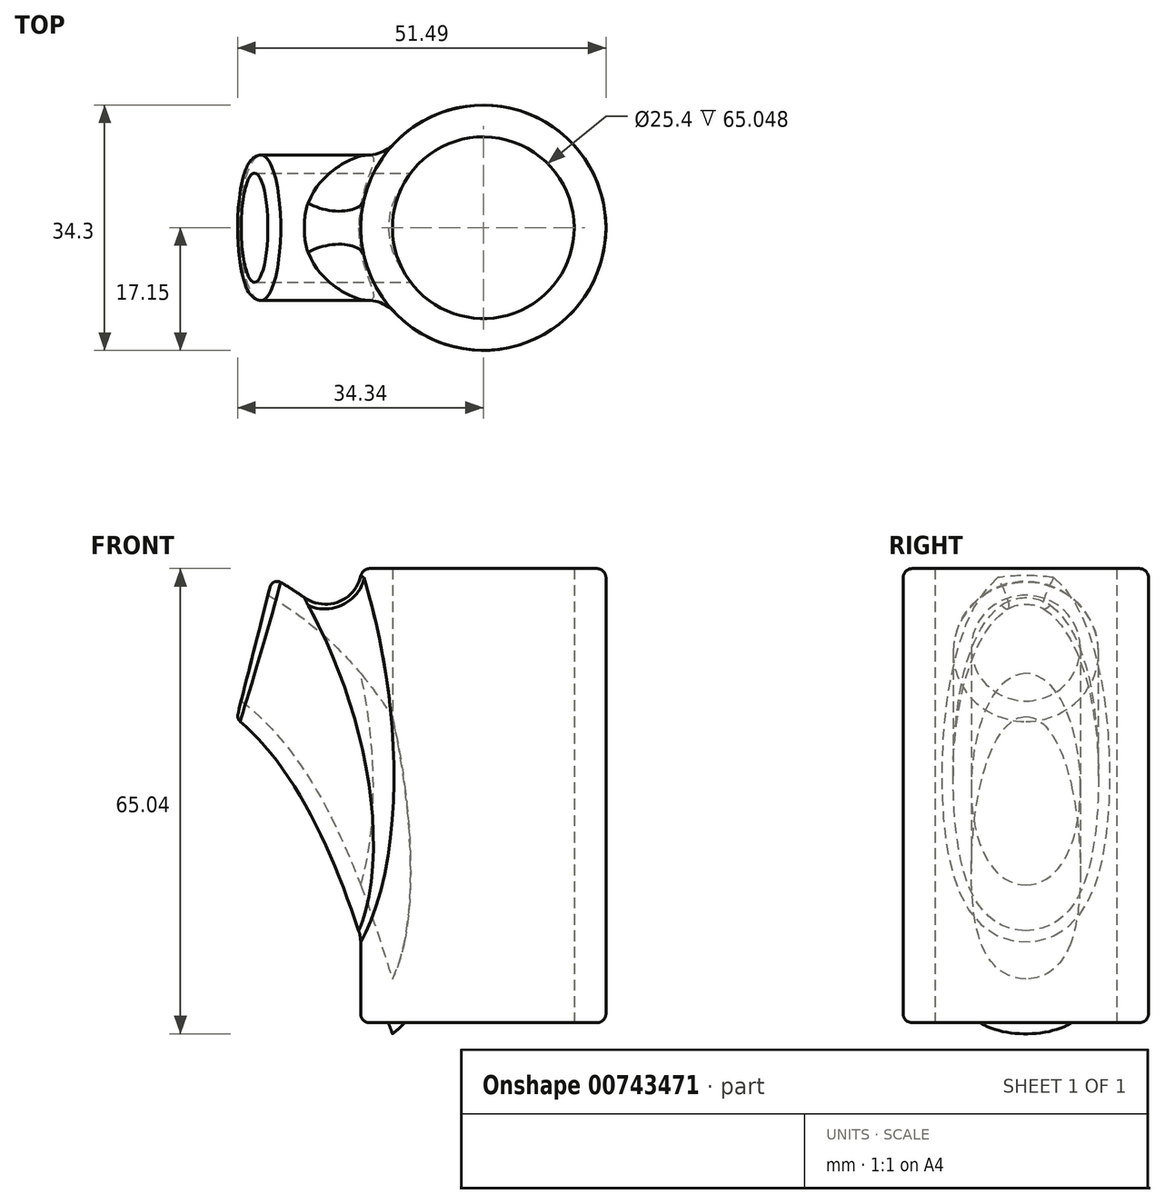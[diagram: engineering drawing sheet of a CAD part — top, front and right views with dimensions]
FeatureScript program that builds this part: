
annotation { "Feature Type Name" : "Feature", "Feature Type Description" : "" }
export const myFeature = defineFeature(function(context is Context, id is Id, definition is map)
    precondition{}
    {
        {
            var Q0;
            Q0=qCreatedBy(makeId("Top.planeOp"),FACE);
            var sketch = newSketch(context, id + "F0", { "sketchPlane" : qUnion([Q0])});
            skCircle(sketch, "E0", {"center": v(0, 0) * mm, "radius": 12.7 * mm});
            skCircle(sketch, "E1", {"center": v(0, 0) * mm, "radius": 17.15 * mm});
            skSolve(sketch);
        }
        {
            var Q0;
            Q0=makeQuery(id+"F0.imprint","IMPRINT",FACE,{"disambiguationData":[TD([[makeQuery(id+"F0.imprint","IMPRINT",EDGE,{"derivedFrom":sQuery(id+"F0.wireOp",EDGE,"E0")}),-1.0]])]});
            extrude(context, id + "F1", {"entities" : qUnion([Q0]), "depth" : 63.5 * mm, "offsetDistance" : 25.4 * mm});
        }
        {
            var Q0;
            Q0=qCreatedBy(makeId("Right.planeOp"),FACE);
            cPlane(context, id + "F2", {"entities" : qUnion([Q0]), "cplaneType" : CPlaneType.OFFSET, "offset" : 16.76 * mm, "oppositeDirection" : true, "width" : 152.4 * mm, "height" : 152.4 * mm});
        }
        {
            var Q0;
            Q0=qCreatedBy(id+"F2.planeOp",FACE);
            var sketch = newSketch(context, id + "F3", { "sketchPlane" : qUnion([Q0])});
            skLineSegment(sketch, "E2", {"start": v(45.22, 63.3) * mm, "end": v(-44.35, 63.3) * mm});
            skSolve(sketch);
        }
        {
            var Q0;
            Q0=sQuery(id+"F3.wireOp",EDGE,"E2");
            cPlane(context, id + "F4", {"entities" : qUnion([Q0]), "cplaneType" : CPlaneType.LINE_ANGLE, "offset" : 25.4 * mm, "angle" : 62.98 * degree, "width" : 152.4 * mm, "height" : 152.4 * mm});
        }
        {
            var Q0;
            Q0=qCreatedBy(id+"F4.planeOp",FACE);
            var sketch = newSketch(context, id + "F5", { "sketchPlane" : qUnion([Q0])});
            skCircle(sketch, "E3", {"center": v(0, 30.29) * mm, "radius": 7.62 * mm});
            skCircle(sketch, "E4", {"center": v(0, 30.29) * mm, "radius": 10.16 * mm});
            skSolve(sketch);
        }
        {
            var Q0;
            {var subQ0=sQuery(id+"F5.wireOp",EDGE,"E4");Q0=makeQuery(id+"FPSWW7IS3d8COEw_1.boolean.opBoolean","SPLIT",FACE,{"disambiguationData":[TD([makeQuery(id+"F1.opExtrude","SWEPT_FACE",FACE,{"disambiguationData":[OSD([sQuery(id+"F0.wireOp",EDGE,"E1")])]})])],"derivedFrom":makeQuery(id+"FPSWW7IS3d8COEw_1.opExtrude","SWEPT_FACE",FACE,{"disambiguationData":[OSD([subQ0])]})});}
            var Q1;
            Q1=makeQuery(id+"F1.opExtrude","CAP_EDGE",EDGE,{"disambiguationData":[OSD([sQuery(id+"F0.wireOp",EDGE,"E1")])],"isStart":false});
            var Q2;
            Q2=makeQuery(id+"F1.opExtrude","CAP_EDGE",EDGE,{"disambiguationData":[OSD([sQuery(id+"F0.wireOp",EDGE,"E1")])],"isStart":true});
            fillet(context, id + "F6", {"entities" : qUnion([Q0, Q1, Q2]), "radius" : 1.27 * mm, "tangentPropagation" : true, "allowEdgeOverflow" : false});
        }
        {
            var Q0;
            Q0=makeQuery(id+"F1.opExtrude","CAP_FACE",FACE,{"disambiguationData":[OSD([sQuery(id+"F0.wireOp",EDGE,"E0"),sQuery(id+"F0.wireOp",EDGE,"E1")])],"isStart":true});
            var sketch = newSketch(context, id + "F7", { "sketchPlane" : qUnion([Q0])});
            skCircle(sketch, "E5", {"center": v(0, 0) * mm, "radius": 12.7 * mm});
            skSolve(sketch);
        }
        {
            var Q0;
            Q0=qSketchRegion(id+"F7",true);
            extrude(context, id + "F8", {"entities" : qUnion([Q0]), "operationType" : NewBodyOperationType.REMOVE, "oppositeDirection" : true, "depth" : 68.07 * mm, "offsetDistance" : 25.4 * mm});
        }
        {
            var Q0;
            Q0=qCreatedBy(makeId("Front.planeOp"),FACE);
            var sketch = newSketch(context, id + "F9", { "sketchPlane" : qUnion([Q0])});
            skPoint(sketch, "E6", {"position": v(-31.9, 52.7) * mm});
            skFitSpline(sketch, "E7", {"points": [v(-32.02, 52.18) * mm, v(-3.1, 0) * mm], "startDerivative": vector(57.73, -37.02) * mm, "endDerivative": vector(13.88, -32.18) * mm});
            skSolve(sketch);
        }
        {
            var Q0;
            Q0=makeQuery(id+"F5.imprint","IMPRINT",FACE,{"disambiguationData":[TD([[makeQuery(id+"F5.imprint","IMPRINT",EDGE,{"derivedFrom":sQuery(id+"F5.wireOp",EDGE,"E3")}),-1.0]])]});
            var Q1;
            Q1=sQuery(id+"F9.wireOp",EDGE,"E7");
            sweep(context, id + "F10", {"operationType" : NewBodyOperationType.ADD, "profiles" : qUnion([Q0]), "path" : qUnion([Q1])});
        }
        {
            var Q0;
            Q0=makeQuery(id+"F1.opExtrude","CAP_FACE",FACE,{"disambiguationData":[OSD([sQuery(id+"F0.wireOp",EDGE,"E0"),sQuery(id+"F0.wireOp",EDGE,"E1")])],"isStart":true});
            var sketch = newSketch(context, id + "F11", { "sketchPlane" : qUnion([Q0])});
            skCircle(sketch, "E8", {"center": v(0, 0) * mm, "radius": 12.7 * mm});
            skSolve(sketch);
        }
        {
            var Q0;
            Q0=qSketchRegion(id+"F11",true);
            extrude(context, id + "F12", {"entities" : qUnion([Q0]), "operationType" : NewBodyOperationType.REMOVE, "oppositeDirection" : true, "depth" : 47.75 * mm, "offsetDistance" : 25.4 * mm, "hasSecondDirection" : true, "secondDirectionOppositeDirection" : false, "secondDirectionDepth" : 25.4 * mm});
        }
        {
            var Q0;
            Q0=makeQuery(id+"F10.opSweep","CAP_FACE",FACE,{"disambiguationData":[OSD([sQuery(id+"F5.wireOp",EDGE,"E3"),sQuery(id+"F5.wireOp",EDGE,"E4"),sQuery(id+"F9.wireOp",VERTEX,"E7.start")])],"isStart":true});
            var sketch = newSketch(context, id + "F13", { "sketchPlane" : qUnion([Q0])});
            skCircle(sketch, "E9", {"center": v(0, 42.94) * mm, "radius": 7.62 * mm});
            skSolve(sketch);
        }
        {
            var Q0;
            Q0=makeQuery(id+"F13.imprint","IMPRINT",FACE,{"disambiguationData":[TD([[makeQuery(id+"F13.imprint","IMPRINT",EDGE,{"derivedFrom":sQuery(id+"F13.wireOp",EDGE,"E9")}),-1.0]])]});
            var Q1;
            Q1=sQuery(id+"F9.wireOp",EDGE,"E7");
            sweep(context, id + "F14", {"operationType" : NewBodyOperationType.REMOVE, "profiles" : qUnion([Q0]), "path" : qUnion([Q1])});
        }
        {
            var Q0;
            Q0=makeQuery(id+"F10.opSweep","CAP_EDGE",EDGE,{"disambiguationData":[OSD([sQuery(id+"F5.wireOp",EDGE,"E4"),sQuery(id+"F9.wireOp",VERTEX,"E7.start")])],"isStart":true});
            fillet(context, id + "F15", {"entities" : qUnion([Q0]), "radius" : 1.02 * mm, "tangentPropagation" : true, "allowEdgeOverflow" : false});
        }
        {
            var Q0;
            Q0=makeQuery(id+"F10.boolean.opBoolean","INTERSECT",EDGE,{"derivedFrom":[makeQuery(id+"F1.opExtrude","SWEPT_FACE",FACE,{"disambiguationData":[OSD([sQuery(id+"F0.wireOp",EDGE,"E1")])]}),makeQuery(id+"F10.opSweep","SWEPT_FACE",FACE,{"disambiguationData":[OSD([sQuery(id+"F5.wireOp",EDGE,"E4"),sQuery(id+"F9.wireOp",EDGE,"E7")])]})]});
            fillet(context, id + "F16", {"entities" : qUnion([Q0]), "radius" : 5.08 * mm, "tangentPropagation" : true, "allowEdgeOverflow" : false});
        }
    });
